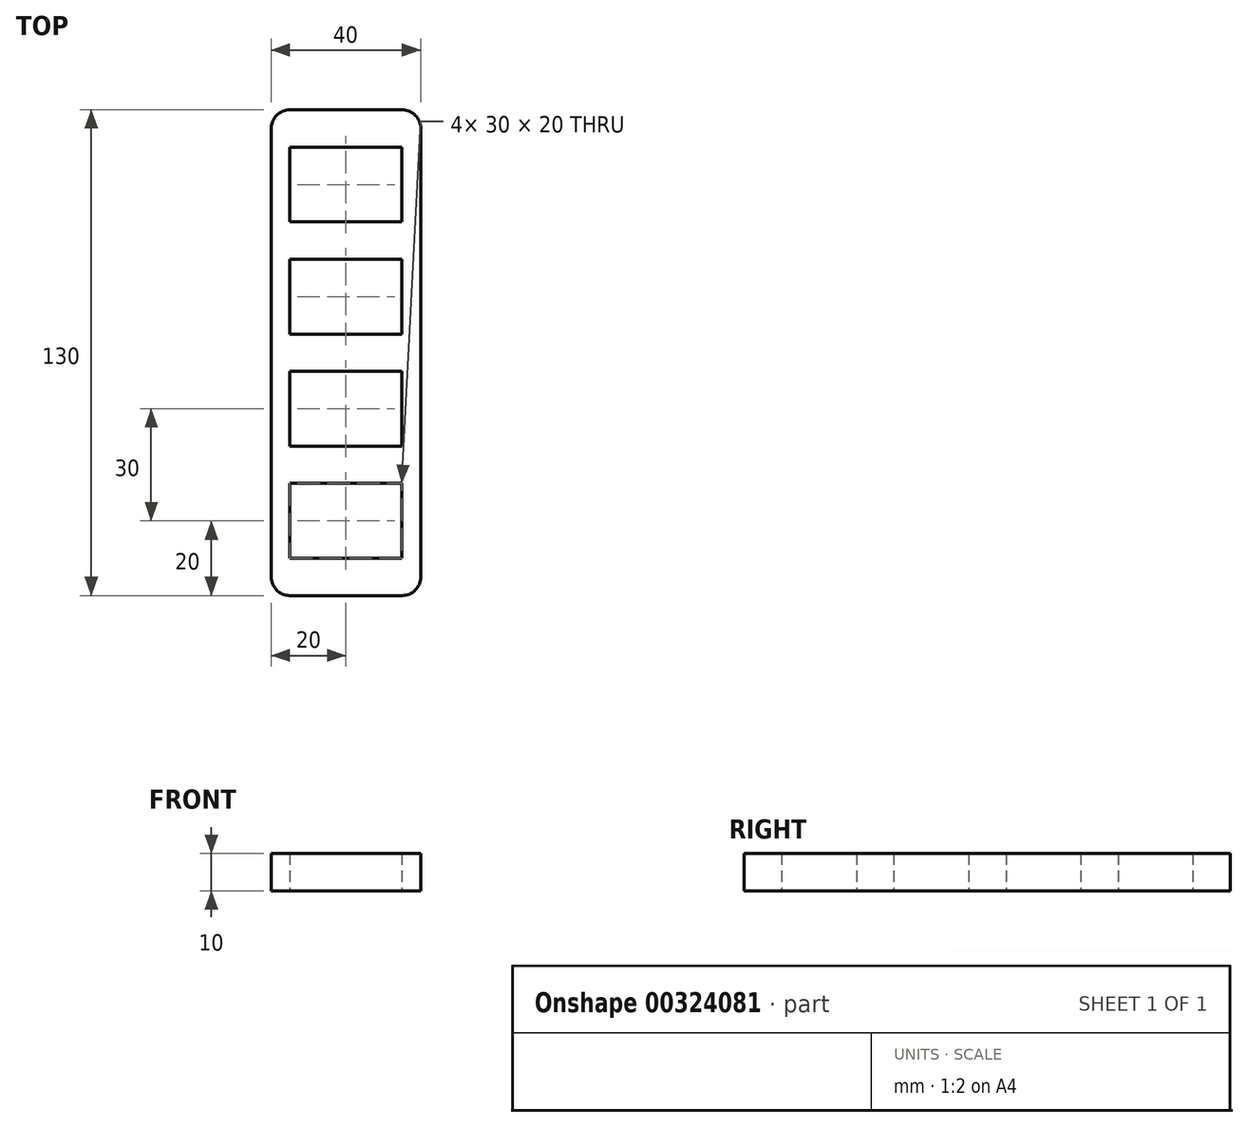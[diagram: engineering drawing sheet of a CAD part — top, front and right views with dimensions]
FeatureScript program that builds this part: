
annotation { "Feature Type Name" : "Feature", "Feature Type Description" : "" }
export const myFeature = defineFeature(function(context is Context, id is Id, definition is map)
    precondition{}
    {
        {
            var Q0;
            Q0=qCreatedBy(makeId("Top.planeOp"),FACE);
            var sketch = newSketch(context, id + "F0", { "sketchPlane" : qUnion([Q0])});
            skLineSegment(sketch, "E0.bottom", {"start": v(70, 70) * mm, "end": v(-70, 70) * mm});
            skLineSegment(sketch, "E0.top", {"start": v(70, -70) * mm, "end": v(-70, -70) * mm});
            skLineSegment(sketch, "E0.left", {"start": v(70, 70) * mm, "end": v(70, -70) * mm});
            skLineSegment(sketch, "E0.right", {"start": v(-70, 70) * mm, "end": v(-70, -70) * mm});
            skPoint(sketch, "E0.middle", {"position": v(0, 0) * mm});
            skLineSegment(sketch, "E1.bottom", {"start": v(-20, 65) * mm, "end": v(20, 65) * mm});
            skLineSegment(sketch, "E1.top", {"start": v(-20, -65) * mm, "end": v(20, -65) * mm});
            skLineSegment(sketch, "E1.left", {"start": v(-20, 65) * mm, "end": v(-20, -65) * mm});
            skLineSegment(sketch, "E1.right", {"start": v(20, 65) * mm, "end": v(20, -65) * mm});
            skSolve(sketch);
        }
        {
            var Q0;
            Q0=makeQuery(id+"F0.imprint","IMPRINT",FACE,{"disambiguationData":[TD([[makeQuery(id+"F0.imprint","IMPRINT",EDGE,{"derivedFrom":sQuery(id+"F0.wireOp",EDGE,"E1.bottom")}),-1.0]])]});
            extrude(context, id + "F1", {"entities" : qUnion([Q0]), "depth" : 10 * mm});
        }
        {
            var Q0;
            Q0=makeQuery(id+"F1.opExtrude","SWEPT_EDGE",EDGE,{"disambiguationData":[OSD([sQuery(id+"F0.wireOp",EDGE,"E1.top"),sQuery(id+"F0.wireOp",EDGE,"E1.left")])]});
            var Q1;
            Q1=makeQuery(id+"F1.opExtrude","SWEPT_EDGE",EDGE,{"disambiguationData":[OSD([sQuery(id+"F0.wireOp",EDGE,"E1.top"),sQuery(id+"F0.wireOp",EDGE,"E1.right")])]});
            var Q2;
            Q2=makeQuery(id+"F1.opExtrude","SWEPT_EDGE",EDGE,{"disambiguationData":[OSD([sQuery(id+"F0.wireOp",EDGE,"E1.bottom"),sQuery(id+"F0.wireOp",EDGE,"E1.right")])]});
            var Q3;
            Q3=makeQuery(id+"F1.opExtrude","SWEPT_EDGE",EDGE,{"disambiguationData":[OSD([sQuery(id+"F0.wireOp",EDGE,"E1.bottom"),sQuery(id+"F0.wireOp",EDGE,"E1.left")])]});
            fillet(context, id + "F2", {"entities" : qUnion([Q0, Q1, Q2, Q3]), "radius" : 5 * mm, "tangentPropagation" : true, "allowEdgeOverflow" : false});
        }
        {
            var Q0;
            Q0=qCreatedBy(makeId("Top.planeOp"),FACE);
            var sketch = newSketch(context, id + "F3", { "sketchPlane" : qUnion([Q0])});
            skLineSegment(sketch, "E2.bottom", {"start": v(-15, 25) * mm, "end": v(15, 25) * mm});
            skLineSegment(sketch, "E2.top", {"start": v(-15, 5) * mm, "end": v(15, 5) * mm});
            skLineSegment(sketch, "E2.left", {"start": v(-15, 25) * mm, "end": v(-15, 5) * mm});
            skLineSegment(sketch, "E2.right", {"start": v(15, 25) * mm, "end": v(15, 5) * mm});
            skPoint(sketch, "E2.middle", {"position": v(0, 15) * mm});
            skLineSegment(sketch, "E3.bottom", {"start": v(-15, 55) * mm, "end": v(15, 55) * mm});
            skLineSegment(sketch, "E3.top", {"start": v(-15, 35) * mm, "end": v(15, 35) * mm});
            skLineSegment(sketch, "E3.left", {"start": v(-15, 55) * mm, "end": v(-15, 35) * mm});
            skLineSegment(sketch, "E3.right", {"start": v(15, 55) * mm, "end": v(15, 35) * mm});
            skPoint(sketch, "E3.middle", {"position": v(0, 45) * mm});
            skLineSegment(sketch, "E4", {"start": v(-38.73, 0) * mm, "end": v(36.02, 0) * mm, "construction": true});
            skLineSegment(sketch, "E5.MirrorCS", {"start": v(15, -25) * mm, "end": v(15, -5) * mm});
            skLineSegment(sketch, "E6.MirrorCS", {"start": v(-15, -25) * mm, "end": v(-15, -5) * mm});
            skLineSegment(sketch, "E7.MirrorCS", {"start": v(-15, -5) * mm, "end": v(15, -5) * mm});
            skLineSegment(sketch, "E8.MirrorCS", {"start": v(-15, -25) * mm, "end": v(15, -25) * mm});
            skLineSegment(sketch, "E9.MirrorCS", {"start": v(-15, -35) * mm, "end": v(15, -35) * mm});
            skLineSegment(sketch, "E10.MirrorCS", {"start": v(-15, -55) * mm, "end": v(-15, -35) * mm});
            skLineSegment(sketch, "E11.MirrorCS", {"start": v(15, -55) * mm, "end": v(15, -35) * mm});
            skLineSegment(sketch, "E12.MirrorCS", {"start": v(-15, -55) * mm, "end": v(15, -55) * mm});
            skSolve(sketch);
        }
        {
            var Q0;
            Q0 = qSketchRegion(id + "F3", true);
            extrude(context, id + "F4", {"entities" : qUnion([Q0]), "operationType" : NewBodyOperationType.REMOVE, "depth" : 25 * mm});
        }
    });
